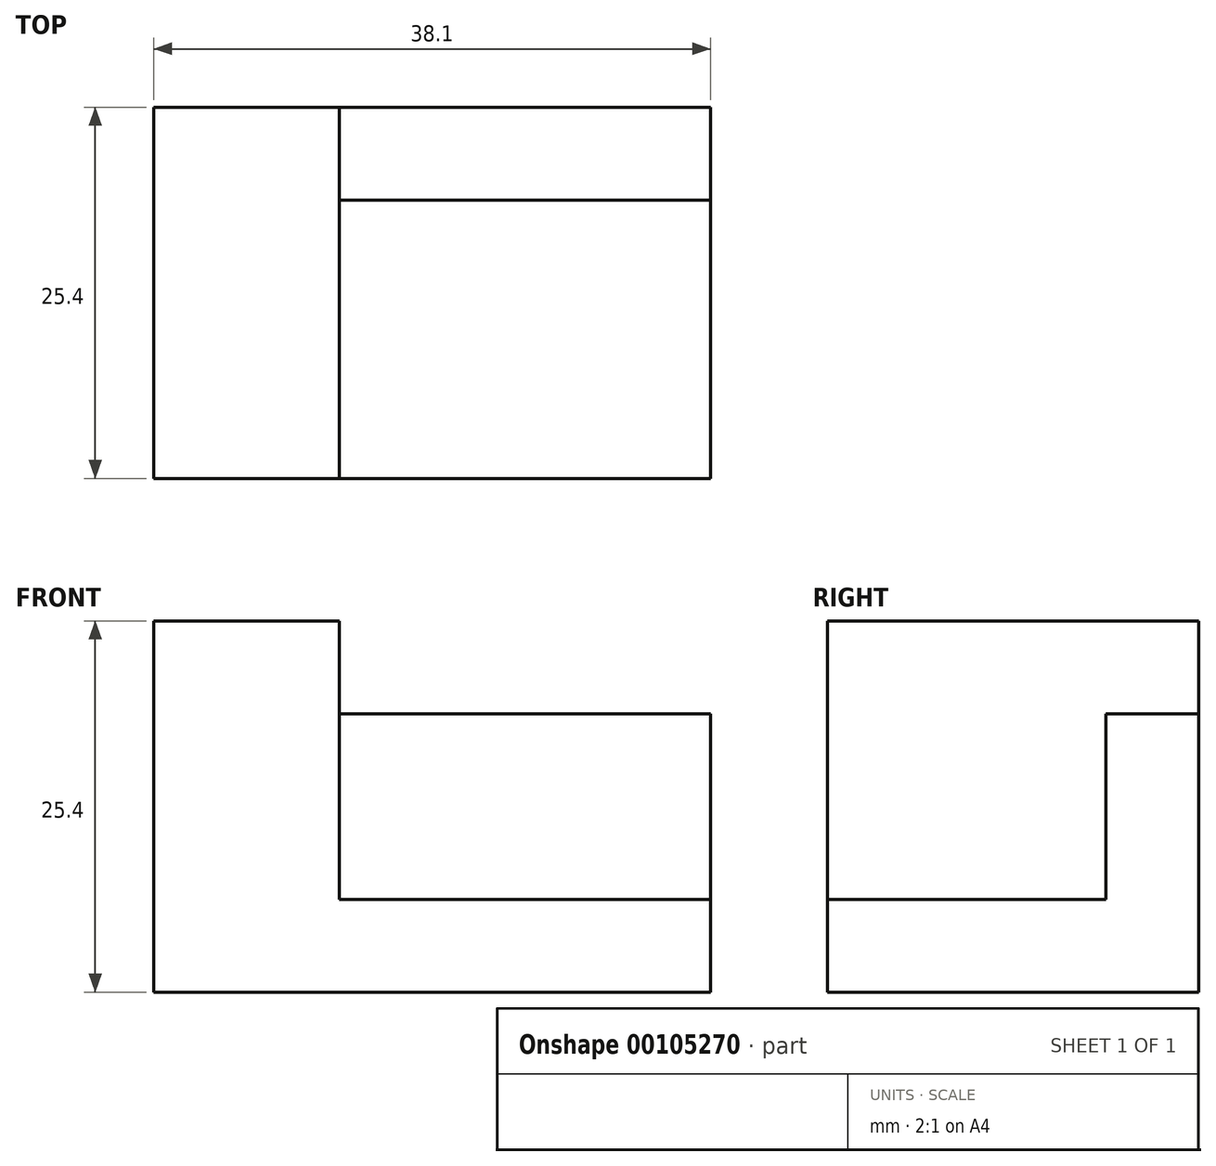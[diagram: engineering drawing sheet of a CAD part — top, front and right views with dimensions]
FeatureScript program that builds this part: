
annotation { "Feature Type Name" : "Feature", "Feature Type Description" : "" }
export const myFeature = defineFeature(function(context is Context, id is Id, definition is map)
    precondition{}
    {
        {
            var Q0;
            Q0=qCreatedBy(makeId("Front.planeOp"),FACE);
            var sketch = newSketch(context, id + "F0", { "sketchPlane" : qUnion([Q0])});
            skLineSegment(sketch, "E0.bottom", {"start": v(0, 0) * mm, "end": v(38.1, 0) * mm});
            skLineSegment(sketch, "E0.top", {"start": v(0, 25.4) * mm, "end": v(12.7, 25.4) * mm});
            skLineSegment(sketch, "E0.left", {"start": v(0, 0) * mm, "end": v(0, 25.4) * mm});
            skLineSegment(sketch, "E0.right", {"start": v(38.1, 0) * mm, "end": v(38.1, 6.35) * mm});
            skLineSegment(sketch, "E1.left", {"start": v(12.7, 6.35) * mm, "end": v(12.7, 25.4) * mm});
            skPoint(sketch, "E1.right.end.orphan", {"position": v(38.1, 25.4) * mm});
            skLineSegment(sketch, "E2", {"start": v(12.7, 6.35) * mm, "end": v(38.1, 6.35) * mm});
            skSolve(sketch);
        }
        {
            var Q0;
            Q0=makeQuery(id+"F0.imprint","IMPRINT",FACE,{"disambiguationData":[TD([[makeQuery(id+"F0.imprint","IMPRINT",EDGE,{"derivedFrom":sQuery(id+"F0.wireOp",EDGE,"E0.bottom")}),1.0]])]});
            extrude(context, id + "F1", {"entities" : qUnion([Q0]), "oppositeDirection" : true, "depth" : 25.4 * mm});
        }
        {
            var Q0;
            Q0=makeQuery(id+"F1.opExtrude","CAP_FACE",FACE,{"disambiguationData":[OSD([sQuery(id+"F0.wireOp",EDGE,"E0.bottom"),sQuery(id+"F0.wireOp",EDGE,"E0.top"),sQuery(id+"F0.wireOp",EDGE,"E0.left"),sQuery(id+"F0.wireOp",EDGE,"E0.right"),sQuery(id+"F0.wireOp",EDGE,"E1.left"),sQuery(id+"F0.wireOp",EDGE,"E2")])],"isStart":false});
            var sketch = newSketch(context, id + "F2", { "sketchPlane" : qUnion([Q0])});
            skLineSegment(sketch, "E3.bottom", {"start": v(-38.1, 6.35) * mm, "end": v(-12.7, 6.35) * mm});
            skLineSegment(sketch, "E3.top", {"start": v(-38.1, 19.05) * mm, "end": v(-12.7, 19.05) * mm});
            skLineSegment(sketch, "E3.left", {"start": v(-38.1, 6.35) * mm, "end": v(-38.1, 19.05) * mm});
            skLineSegment(sketch, "E3.right", {"start": v(-12.7, 6.35) * mm, "end": v(-12.7, 19.05) * mm});
            skSolve(sketch);
        }
        {
            var Q0;
            Q0=makeQuery(id+"F2.imprint","IMPRINT",FACE,{"disambiguationData":[TD([[makeQuery(id+"F2.imprint","IMPRINT",EDGE,{"derivedFrom":sQuery(id+"F2.wireOp",EDGE,"E3.bottom")}),-1.0]])]});
            extrude(context, id + "F3", {"entities" : qUnion([Q0]), "operationType" : NewBodyOperationType.ADD, "oppositeDirection" : true, "depth" : 6.35 * mm});
        }
    });
